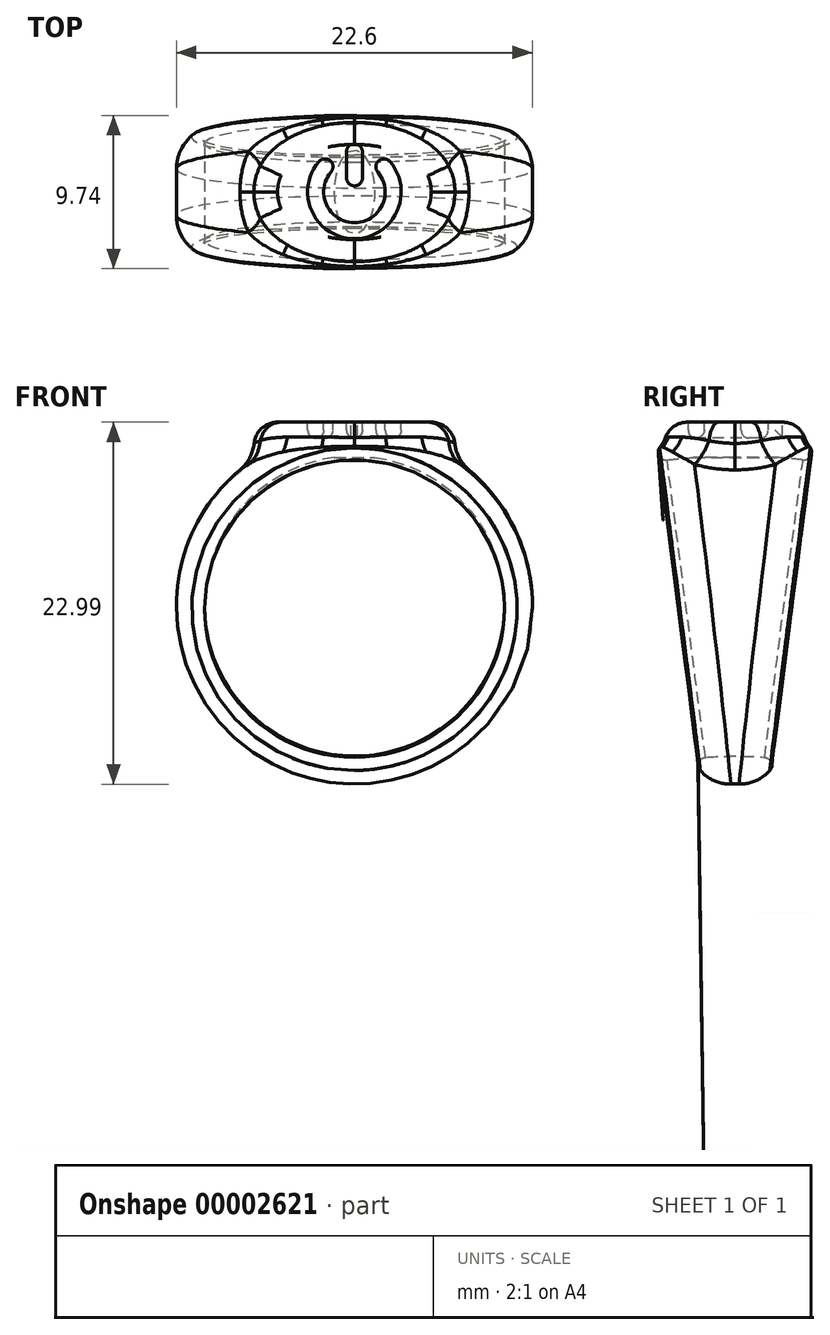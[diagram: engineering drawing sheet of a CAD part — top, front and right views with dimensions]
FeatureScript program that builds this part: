
annotation { "Feature Type Name" : "Feature", "Feature Type Description" : "" }
export const myFeature = defineFeature(function(context is Context, id is Id, definition is map)
    precondition{}
    {
        {
            var Q0;
            Q0=qCreatedBy(makeId("Front.planeOp"),FACE);
            var sketch = newSketch(context, id + "F0", { "sketchPlane" : qUnion([Q0])});
            skCircle(sketch, "E0", {"center": v(0, 0) * mm, "radius": 9.52 * mm});
            skCircle(sketch, "E1", {"center": v(0, 0) * mm, "radius": 11.3 * mm});
            skLineSegment(sketch, "E2", {"start": v(-19.06, -29.92) * mm, "end": v(20.06, -29.92) * mm, "construction": true});
            skSolve(sketch);
        }
        {
            var Q0;
            Q0=makeQuery(id+"F0.imprint","IMPRINT",FACE,{"disambiguationData":[TD([[makeQuery(id+"F0.imprint","IMPRINT",EDGE,{"derivedFrom":sQuery(id+"F0.wireOp",EDGE,"E0")}),-1.0]])]});
            var Q1;
            Q1=sQuery(id+"F0.wireOp",EDGE,"E2");
            revolve(context, id + "F1", {"entities" : qUnion([Q0]), "axis" : qUnion([Q1]), "revolveType" : RevolveType.SYMMETRIC, "angle" : 15 * degree});
        }
        {
            var Q0;
            Q0=qCreatedBy(makeId("Top.planeOp"),FACE);
            cPlane(context, id + "F2", {"entities" : qUnion([Q0]), "cplaneType" : CPlaneType.OFFSET, "offset" : 11.68 * mm, "width" : 152.4 * mm, "height" : 152.4 * mm});
        }
        {
            var Q0;
            Q0=qCreatedBy(id+"F2.planeOp",FACE);
            var sketch = newSketch(context, id + "F3", { "sketchPlane" : qUnion([Q0])});
            skLineSegment(sketch, "E3", {"start": v(-13.16, 0) * mm, "end": v(13.94, 0) * mm, "construction": true});
            skLineSegment(sketch, "E4", {"start": v(0, 6.68) * mm, "end": v(0, -7.16) * mm, "construction": true});
            skFitSpline(sketch, "E5", {"points": [v(-6.35, 0) * mm, v(0, 4.24) * mm], "startDerivative": vector(-0.42, 8.09) * mm, "endDerivative": vector(8.17, -0.21) * mm});
            skFitSpline(sketch, "E6.0.MirrorCS", {"points": [v(6.35, 0) * mm, v(0, 4.24) * mm], "startDerivative": vector(0.42, 8.09) * mm, "endDerivative": vector(-8.17, -0.21) * mm});
            skFitSpline(sketch, "E7.0.MirrorCS", {"points": [v(-6.35, 0) * mm, v(0, -4.24) * mm], "startDerivative": vector(-0.42, -8.09) * mm, "endDerivative": vector(8.17, 0.21) * mm});
            skFitSpline(sketch, "E8.0.MirrorCS", {"points": [v(6.35, 0) * mm, v(0, -4.24) * mm], "startDerivative": vector(0.42, -8.09) * mm, "endDerivative": vector(-8.17, 0.21) * mm});
            skSolve(sketch);
        }
        {
            var Q0;
            Q0=makeQuery(id+"F3.imprint","IMPRINT",FACE,{"disambiguationData":[TD([[makeQuery(id+"F3.imprint","IMPRINT",EDGE,{"derivedFrom":sQuery(id+"F3.wireOp",EDGE,"E5")}),-1.0]])]});
            extrude(context, id + "F4", {"entities" : qUnion([Q0]), "operationType" : NewBodyOperationType.ADD, "oppositeDirection" : true, "depth" : 2.25 * mm});
        }
        {
            var Q0;
            Q0=makeQuery(id+"F1.opRevolve","CAP_EDGE",EDGE,{"disambiguationData":[OSD([sQuery(id+"F0.wireOp",EDGE,"E1")])],"isStart":false});
            var Q1;
            Q1=makeQuery(id+"F1.opRevolve","CAP_EDGE",EDGE,{"disambiguationData":[OSD([sQuery(id+"F0.wireOp",EDGE,"E1")])],"isStart":true});
            fillet(context, id + "F5", {"entities" : qUnion([Q0, Q1]), "radius" : 2.54 * mm, "tangentPropagation" : true, "allowEdgeOverflow" : false});
        }
        {
            var Q0;
            Q0=makeQuery(id+"F5.opFillet","BLEND_EDGE",EDGE,{"blendedFrom":[makeQuery(id+"F1.opRevolve","CAP_EDGE",EDGE,{"disambiguationData":[OSD([sQuery(id+"F0.wireOp",EDGE,"E1")])],"isStart":false}),makeQuery(id+"F4.opExtrude","SWEPT_FACE",FACE,{"disambiguationData":[OSD([sQuery(id+"F3.wireOp",EDGE,"E7.0.MirrorCS")])]})],"blendedInto":[makeQuery(id+"F4.opExtrude","SWEPT_FACE",FACE,{"disambiguationData":[OSD([sQuery(id+"F3.wireOp",EDGE,"E7.0.MirrorCS")])]})]});
            var Q1;
            Q1=makeQuery(id+"F5.opFillet","BLEND_EDGE",EDGE,{"blendedFrom":[makeQuery(id+"F1.opRevolve","CAP_EDGE",EDGE,{"disambiguationData":[OSD([sQuery(id+"F0.wireOp",EDGE,"E1")])],"isStart":false}),makeQuery(id+"F4.opExtrude","SWEPT_FACE",FACE,{"disambiguationData":[OSD([sQuery(id+"F3.wireOp",EDGE,"E8.0.MirrorCS")])]})],"blendedInto":[makeQuery(id+"F4.opExtrude","SWEPT_FACE",FACE,{"disambiguationData":[OSD([sQuery(id+"F3.wireOp",EDGE,"E8.0.MirrorCS")])]})]});
            var Q2;
            Q2=makeQuery(id+"F4.boolean.opBoolean","INTERSECT",EDGE,{"derivedFrom":[makeQuery(id+"F1.opRevolve","SWEPT_FACE",FACE,{"disambiguationData":[OSD([sQuery(id+"F0.wireOp",EDGE,"E1")])]}),makeQuery(id+"F4.opExtrude","SWEPT_FACE",FACE,{"disambiguationData":[OSD([sQuery(id+"F3.wireOp",EDGE,"E8.0.MirrorCS")])]})]});
            var Q3;
            Q3=makeQuery(id+"F4.opExtrude","CAP_EDGE",EDGE,{"disambiguationData":[OSD([sQuery(id+"F3.wireOp",EDGE,"E7.0.MirrorCS")])],"isStart":false});
            var Q4;
            Q4=makeQuery(id+"F4.opExtrude","CAP_EDGE",EDGE,{"disambiguationData":[OSD([sQuery(id+"F3.wireOp",EDGE,"E5")])],"isStart":false});
            var Q5;
            Q5=makeQuery(id+"F4.boolean.opBoolean","INTERSECT",EDGE,{"derivedFrom":[makeQuery(id+"F1.opRevolve","SWEPT_FACE",FACE,{"disambiguationData":[OSD([sQuery(id+"F0.wireOp",EDGE,"E1")])]}),makeQuery(id+"F4.opExtrude","SWEPT_FACE",FACE,{"disambiguationData":[OSD([sQuery(id+"F3.wireOp",EDGE,"E5")])]})]});
            var Q6;
            Q6=makeQuery(id+"F5.opFillet","BLEND_EDGE",EDGE,{"blendedFrom":[makeQuery(id+"F1.opRevolve","CAP_EDGE",EDGE,{"disambiguationData":[OSD([sQuery(id+"F0.wireOp",EDGE,"E1")])],"isStart":true}),makeQuery(id+"F4.opExtrude","SWEPT_FACE",FACE,{"disambiguationData":[OSD([sQuery(id+"F3.wireOp",EDGE,"E5")])]})],"blendedInto":[makeQuery(id+"F4.opExtrude","SWEPT_FACE",FACE,{"disambiguationData":[OSD([sQuery(id+"F3.wireOp",EDGE,"E5")])]})]});
            var Q7;
            Q7=makeQuery(id+"F5.opFillet","BLEND_EDGE",EDGE,{"blendedFrom":[makeQuery(id+"F1.opRevolve","CAP_EDGE",EDGE,{"disambiguationData":[OSD([sQuery(id+"F0.wireOp",EDGE,"E1")])],"isStart":true}),makeQuery(id+"F4.opExtrude","SWEPT_FACE",FACE,{"disambiguationData":[OSD([sQuery(id+"F3.wireOp",EDGE,"E6.0.MirrorCS")])]})],"blendedInto":[makeQuery(id+"F4.opExtrude","SWEPT_FACE",FACE,{"disambiguationData":[OSD([sQuery(id+"F3.wireOp",EDGE,"E6.0.MirrorCS")])]})]});
            fillet(context, id + "F6", {"entities" : qUnion([Q0, Q1, Q2, Q3, Q4, Q5, Q6, Q7]), "radius" : 2.54 * mm, "tangentPropagation" : true, "allowEdgeOverflow" : false});
        }
        {
            var Q0;
            {var subQ0=makeQuery(id+"F4.opExtrude","CAP_EDGE",EDGE,{"disambiguationData":[OSD([sQuery(id+"F3.wireOp",EDGE,"E7.0.MirrorCS")])],"isStart":true});Q0=qUnion([subQ0,subQ0]);}
            var Q1;
            {var subQ0=makeQuery(id+"F4.opExtrude","CAP_EDGE",EDGE,{"disambiguationData":[OSD([sQuery(id+"F3.wireOp",EDGE,"E5")])],"isStart":true});Q1=qUnion([subQ0,subQ0]);}
            var Q2;
            {var subQ0=makeQuery(id+"F4.opExtrude","CAP_EDGE",EDGE,{"disambiguationData":[OSD([sQuery(id+"F3.wireOp",EDGE,"E8.0.MirrorCS")])],"isStart":true});Q2=qUnion([subQ0,subQ0]);}
            var Q3;
            {var subQ0=makeQuery(id+"F4.opExtrude","CAP_EDGE",EDGE,{"disambiguationData":[OSD([sQuery(id+"F3.wireOp",EDGE,"E6.0.MirrorCS")])],"isStart":true});Q3=qUnion([subQ0,subQ0]);}
            fillet(context, id + "F7", {"entities" : qUnion([Q0, Q1, Q2, Q3]), "radius" : 1.5 * mm, "tangentPropagation" : true, "allowEdgeOverflow" : false});
        }
        {
            var Q0;
            Q0=makeQuery(id+"F4.opExtrude","CAP_FACE",FACE,{"disambiguationData":[OSD([sQuery(id+"F3.wireOp",EDGE,"E5"),sQuery(id+"F3.wireOp",EDGE,"E6.0.MirrorCS"),sQuery(id+"F3.wireOp",EDGE,"E7.0.MirrorCS"),sQuery(id+"F3.wireOp",EDGE,"E8.0.MirrorCS")])],"isStart":true});
            var sketch = newSketch(context, id + "F8", { "sketchPlane" : qUnion([Q0])});
            skArc(sketch, "E9", {"start": v(-1.48, 1.27) * mm, "mid": v(0, -1.95) * mm, "end": v(1.48, 1.27) * mm});
            skArc(sketch, "E10", {"start": v(-2.25, 1.93) * mm, "mid": v(0, -2.97) * mm, "end": v(2.25, 1.93) * mm});
            skLineSegment(sketch, "E11", {"start": v(-1.47, 1.91) * mm, "end": v(-1.47, 1.91) * mm});
            skLineSegment(sketch, "E12", {"start": v(1.47, 1.91) * mm, "end": v(1.47, 1.91) * mm});
            skLineSegment(sketch, "E13", {"start": v(0, -3.6) * mm, "end": v(0, 3.87) * mm, "construction": true});
            skPoint(sketch, "E14.orphan", {"position": v(-2.72, 3.55) * mm});
            skPoint(sketch, "E15.orphan", {"position": v(2.72, 3.55) * mm});
            skPoint(sketch, "E16.visualSharp", {"position": v(-1.8, 2.36) * mm});
            skArc(sketch, "E16.filletArc", {"start": v(-1.47, 1.91) * mm, "mid": v(-1.86, 2.1) * mm, "end": v(-2.25, 1.93) * mm});
            skPoint(sketch, "E17.visualSharp", {"position": v(-1.19, 1.55) * mm});
            skArc(sketch, "E17.filletArc", {"start": v(-1.48, 1.27) * mm, "mid": v(-1.36, 1.59) * mm, "end": v(-1.47, 1.91) * mm});
            skPoint(sketch, "E18.visualSharp", {"position": v(1.19, 1.55) * mm});
            skArc(sketch, "E18.filletArc", {"start": v(1.47, 1.91) * mm, "mid": v(1.36, 1.59) * mm, "end": v(1.48, 1.27) * mm});
            skPoint(sketch, "E19.visualSharp", {"position": v(1.8, 2.36) * mm});
            skArc(sketch, "E19.filletArc", {"start": v(2.25, 1.93) * mm, "mid": v(1.86, 2.1) * mm, "end": v(1.47, 1.91) * mm});
            skLineSegment(sketch, "E20", {"start": v(-0.5, 2.55) * mm, "end": v(-0.5, 0.9) * mm});
            skArc(sketch, "E21", {"start": v(-0.5, 0.9) * mm, "mid": v(0, 0.4) * mm, "end": v(0.5, 0.9) * mm});
            skArc(sketch, "E22", {"start": v(0.5, 2.55) * mm, "mid": v(0, 3.06) * mm, "end": v(-0.5, 2.55) * mm});
            skLineSegment(sketch, "E23.0.MirrorCS", {"start": v(0.5, 2.55) * mm, "end": v(0.5, 0.9) * mm});
            skSolve(sketch);
        }
        {
            var Q0;
            Q0=makeQuery(id+"F8.imprint","IMPRINT",FACE,{"disambiguationData":[TD([[makeQuery(id+"F8.imprint","IMPRINT",EDGE,{"derivedFrom":sQuery(id+"F8.wireOp",EDGE,"E9")}),-1.0]])]});
            var Q1;
            {var subQ10=sQuery(id+"F8.wireOp",EDGE,"E20");Q1=makeQuery(id+"F8.imprint","IMPRINT",FACE,{"disambiguationData":[TD([[makeQuery(id+"F8.imprint","IMPRINT",EDGE,{"derivedFrom":subQ10}),1.0]])]});}
            extrude(context, id + "F9", {"entities" : qUnion([Q0, Q1]), "operationType" : NewBodyOperationType.REMOVE, "oppositeDirection" : true, "depth" : 1.02 * mm});
        }
        {
            var Q0;
            Q0=makeQuery(id+"F9.opExtrude","CAP_EDGE",EDGE,{"disambiguationData":[OSD([sQuery(id+"F8.wireOp",EDGE,"E10")])],"isStart":false});
            var Q1;
            Q1=makeQuery(id+"F9.opExtrude","CAP_EDGE",EDGE,{"disambiguationData":[OSD([sQuery(id+"F8.wireOp",EDGE,"E9")])],"isStart":false});
            var Q2;
            Q2=makeQuery(id+"F9.opExtrude","CAP_EDGE",EDGE,{"disambiguationData":[OSD([sQuery(id+"F8.wireOp",EDGE,"E16.filletArc"),sQuery(id+"F8.wireOp",EDGE,"E17.filletArc")])],"isStart":false});
            var Q3;
            Q3=makeQuery(id+"F9.opExtrude","CAP_EDGE",EDGE,{"disambiguationData":[OSD([sQuery(id+"F8.wireOp",EDGE,"E18.filletArc"),sQuery(id+"F8.wireOp",EDGE,"E19.filletArc")])],"isStart":false});
            var Q4;
            Q4=makeQuery(id+"F9.opExtrude","CAP_EDGE",EDGE,{"disambiguationData":[OSD([sQuery(id+"F8.wireOp",EDGE,"E21")])],"isStart":false});
            var Q5;
            Q5=makeQuery(id+"F9.opExtrude","CAP_EDGE",EDGE,{"disambiguationData":[OSD([sQuery(id+"F8.wireOp",EDGE,"E23.0.MirrorCS")])],"isStart":false});
            var Q6;
            Q6=makeQuery(id+"F9.opExtrude","CAP_EDGE",EDGE,{"disambiguationData":[OSD([sQuery(id+"F8.wireOp",EDGE,"E20")])],"isStart":false});
            var Q7;
            Q7=makeQuery(id+"F9.opExtrude","CAP_EDGE",EDGE,{"disambiguationData":[OSD([sQuery(id+"F8.wireOp",EDGE,"E22")])],"isStart":false});
            var Q8;
            Q8=makeQuery(id+"F9.boolean.opBoolean","COPY",EDGE,{"derivedFrom":makeQuery(id+"F9.opExtrude","CAP_EDGE",EDGE,{"disambiguationData":[OSD([sQuery(id+"F8.wireOp",EDGE,"E10")])],"isStart":false})});
            var Q9;
            Q9=makeQuery(id+"F9.boolean.opBoolean","COPY",EDGE,{"derivedFrom":makeQuery(id+"F9.opExtrude","CAP_EDGE",EDGE,{"disambiguationData":[OSD([sQuery(id+"F8.wireOp",EDGE,"E20")])],"isStart":false})});
            fillet(context, id + "F10", {"entities" : qUnion([Q0, Q1, Q2, Q3, Q4, Q5, Q6, Q7, Q8, Q9]), "radius" : 0.5 * mm, "tangentPropagation" : true, "allowEdgeOverflow" : false});
        }
        {
            var Q0;
            Q0=makeQuery(id+"F5.opFillet","BLEND_EDGE",EDGE,{"blendedFrom":[makeQuery(id+"F1.opRevolve","CAP_EDGE",EDGE,{"disambiguationData":[OSD([sQuery(id+"F0.wireOp",EDGE,"E1")])],"isStart":false}),makeQuery(id+"F1.opRevolve","SWEPT_FACE",FACE,{"disambiguationData":[OSD([sQuery(id+"F0.wireOp",EDGE,"E0")])]})],"blendedInto":[makeQuery(id+"F1.opRevolve","SWEPT_FACE",FACE,{"disambiguationData":[OSD([sQuery(id+"F0.wireOp",EDGE,"E0")])]})]});
            var Q1;
            Q1=makeQuery(id+"F5.opFillet","BLEND_EDGE",EDGE,{"blendedFrom":[makeQuery(id+"F1.opRevolve","CAP_EDGE",EDGE,{"disambiguationData":[OSD([sQuery(id+"F0.wireOp",EDGE,"E1")])],"isStart":true}),makeQuery(id+"F1.opRevolve","SWEPT_FACE",FACE,{"disambiguationData":[OSD([sQuery(id+"F0.wireOp",EDGE,"E0")])]})],"blendedInto":[makeQuery(id+"F1.opRevolve","SWEPT_FACE",FACE,{"disambiguationData":[OSD([sQuery(id+"F0.wireOp",EDGE,"E0")])]})]});
            fillet(context, id + "F11", {"entities" : qUnion([Q0, Q1]), "radius" : .5 * mm, "tangentPropagation" : true, "allowEdgeOverflow" : false});
        }
    });
